# Revit family: RL-1-E Rücklaufventil DG 3723
name_source: partatom
category: Rohrzubehör
units: mm (PartAtom-declared; Revit-internal decimal feet)

## family parameters
Arbeitsebenenbasiert = Nein
Beim Laden mit Abzugskörper schneiden = Nein
Bemaßung runder Anschluss = Durchmesser verwenden
Gemeinsam genutzt = Nein
Immer vertikal = Nein
OmniClass-Nummer = 23.65.55.14
OmniClass-Titel = Valves for Liquid Services
Teiletyp = Unterbricht

## types (1)
- RL-1-E Rücklaufventil DG 3723
    Anwendungsgebiet = Wasserheizungsanlagen. Durch den Einbau des Rücklaufventils ist der Heizkörper-Rücklaufanschluß absperrbar. Dadurch kann bei gleichzeitiger Absperrung des Vorlaufventils der Heizkörper bei unter Druck stehender Anlage demontiert werden.
    Ausführungen = Standardmodelle mit Gewindemuffen in vernickelter Ausführung
    Gehäuse = vernickelt
    H03 = 15.5 mm  [stored 0.050853 ft]
    H05 = 17 mm  [stored 0.0557743 ft]
    H07 = 14 mm  [stored 0.0459318 ft]
    H6 = 8 mm  [stored 0.0262467 ft]
    Hersteller = HERZ Armaturen Ges.m.b.H.
    LO1 = 3 mm  [stored 0.00984252 ft]
    LO2 = 19.5 mm  [stored 0.0639764 ft]
    Max.Betriebsdruck = 1000000.0 Pa
    Max.Betriebstemperatur = 120 °C
    Medium = Heizwasserqualität entsprechend ÖNORM H 5195 bzw. VDI-Richtllinie 2035.
    R01 = 18 mm  [stored 0.0590551 ft]
    R02 = 19.5 mm  [stored 0.0639764 ft]
    R03 = 16.5 mm  [stored 0.0541339 ft]
    R04 = 17.5 mm  [stored 0.0574147 ft]
    R05 = 11.75 mm  [stored 0.0385499 ft]
    R06 = 10 mm  [stored 0.0328084 ft]
    S01 = 10 mm  [stored 0.0328084 ft]
    S03 = 61 mm  [stored 0.200131 ft]
    S04 = 45 mm  [stored 0.147638 ft]
    SCRNCODE = 05;01;02
    SCRNSEQ = ARM;ARM_TYP="ALLF";2
    Sitzdichtung = weichdichtend
    Spindelabdichtung = Doppel-O-Ring
    URL = www.herz-armaturen.at
    Vorgabe-Ansicht = 0 mm  [stored 0 ft]

note: [stored X ft] marks values corroborated as IEEE doubles in the binary element streams (Revit-internal decimal feet)
